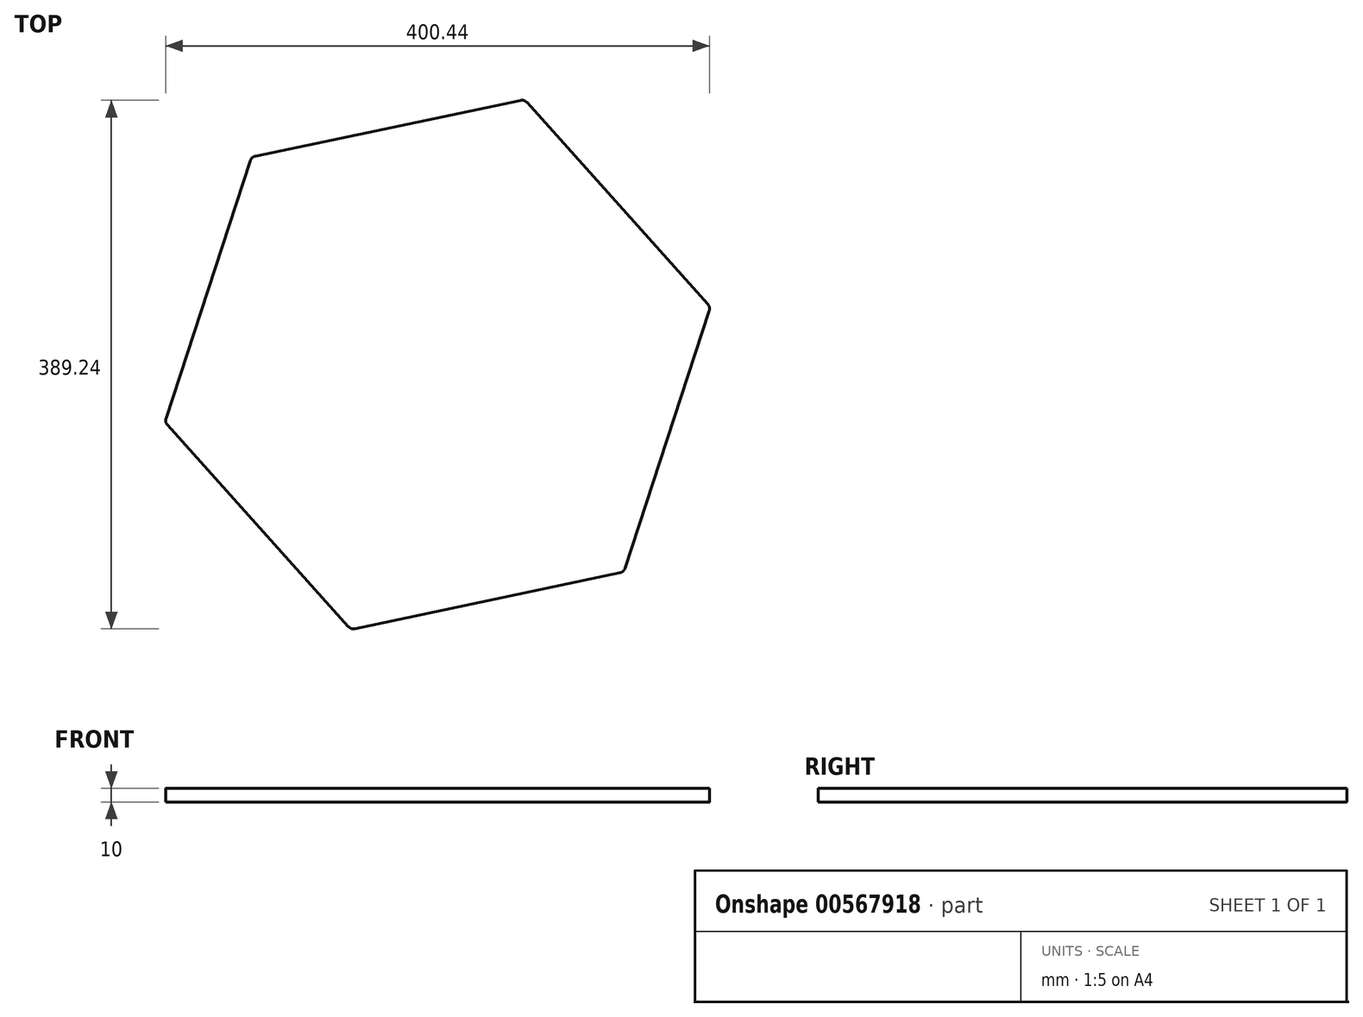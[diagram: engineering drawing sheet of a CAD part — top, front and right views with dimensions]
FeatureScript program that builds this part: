
annotation { "Feature Type Name" : "Feature", "Feature Type Description" : "" }
export const myFeature = defineFeature(function(context is Context, id is Id, definition is map)
    precondition{}
    {
        {
            var Q0;
            Q0=qCreatedBy(makeId("Top.planeOp"),FACE);
            var sketch = newSketch(context, id + "F0", { "sketchPlane" : qUnion([Q0])});
            skCircle(sketch, "E0.cCircle", {"center": v(0, 0) * mm, "radius": 205.28 * mm, "construction": true});
            skLineSegment(sketch, "E0.0", {"start": v(200.88, 42.3) * mm, "end": v(137.07, -152.82) * mm});
            skLineSegment(sketch, "E0.1", {"start": v(137.07, -152.82) * mm, "end": v(-63.8, -195.11) * mm});
            skLineSegment(sketch, "E0.2", {"start": v(-63.8, -195.11) * mm, "end": v(-200.88, -42.3) * mm});
            skLineSegment(sketch, "E0.3", {"start": v(-200.88, -42.3) * mm, "end": v(-137.07, 152.82) * mm});
            skLineSegment(sketch, "E0.4", {"start": v(-137.07, 152.82) * mm, "end": v(63.8, 195.11) * mm});
            skLineSegment(sketch, "E0.5", {"start": v(63.8, 195.11) * mm, "end": v(200.88, 42.3) * mm});
            skSolve(sketch);
        }
        {
            var Q0;
            Q0=makeQuery(id+"F0.imprint","IMPRINT",FACE,{"disambiguationData":[TD([[makeQuery(id+"F0.imprint","IMPRINT",EDGE,{"derivedFrom":sQuery(id+"F0.wireOp",EDGE,"E0.0")}),-1.0]])]});
            extrude(context, id + "F1", {"entities" : qUnion([Q0]), "depth" : 10 * mm, "offsetDistance" : 25.4 * mm});
        }
        {
            var Q0;
            Q0=makeQuery(id+"F1.opExtrude","SWEPT_EDGE",EDGE,{"disambiguationData":[OSD([sQuery(id+"F0.wireOp",EDGE,"E0.1"),sQuery(id+"F0.wireOp",EDGE,"E0.2")])]});
            var Q1;
            Q1=makeQuery(id+"F1.opExtrude","SWEPT_EDGE",EDGE,{"disambiguationData":[OSD([sQuery(id+"F0.wireOp",EDGE,"E0.0"),sQuery(id+"F0.wireOp",EDGE,"E0.1")])]});
            var Q2;
            Q2=makeQuery(id+"F1.opExtrude","SWEPT_EDGE",EDGE,{"disambiguationData":[OSD([sQuery(id+"F0.wireOp",EDGE,"E0.0"),sQuery(id+"F0.wireOp",EDGE,"E0.5")])]});
            var Q3;
            Q3=makeQuery(id+"F1.opExtrude","SWEPT_EDGE",EDGE,{"disambiguationData":[OSD([sQuery(id+"F0.wireOp",EDGE,"E0.2"),sQuery(id+"F0.wireOp",EDGE,"E0.3")])]});
            var Q4;
            Q4=makeQuery(id+"F1.opExtrude","SWEPT_EDGE",EDGE,{"disambiguationData":[OSD([sQuery(id+"F0.wireOp",EDGE,"E0.4"),sQuery(id+"F0.wireOp",EDGE,"E0.5")])]});
            var Q5;
            Q5=makeQuery(id+"F1.opExtrude","SWEPT_EDGE",EDGE,{"disambiguationData":[OSD([sQuery(id+"F0.wireOp",EDGE,"E0.3"),sQuery(id+"F0.wireOp",EDGE,"E0.4")])]});
            fillet(context, id + "F2", {"entities" : qUnion([Q0, Q1, Q2, Q3, Q4, Q5]), "radius" : 5.08 * mm, "tangentPropagation" : true, "allowEdgeOverflow" : false});
        }
    });
